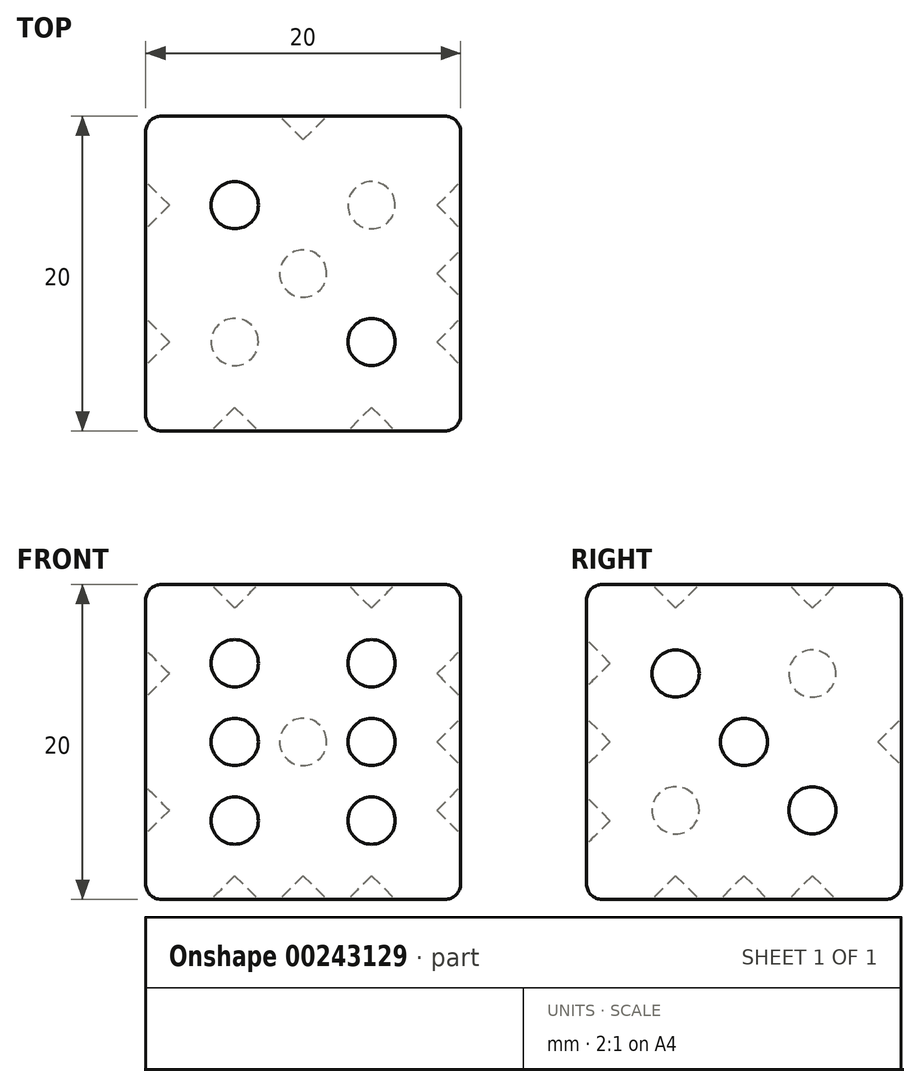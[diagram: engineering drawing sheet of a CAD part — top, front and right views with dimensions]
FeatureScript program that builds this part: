
annotation { "Feature Type Name" : "Feature", "Feature Type Description" : "" }
export const myFeature = defineFeature(function(context is Context, id is Id, definition is map)
    precondition{}
    {
        {
            var Q0;
            Q0=qCreatedBy(makeId("Top.planeOp"),FACE);
            var sketch = newSketch(context, id + "F0", { "sketchPlane" : qUnion([Q0])});
            skLineSegment(sketch, "E0.bottom", {"start": v(0, 0) * mm, "end": v(20, 0) * mm});
            skLineSegment(sketch, "E0.top", {"start": v(0, 20) * mm, "end": v(20, 20) * mm});
            skLineSegment(sketch, "E0.left", {"start": v(0, 0) * mm, "end": v(0, 20) * mm});
            skLineSegment(sketch, "E0.right", {"start": v(20, 0) * mm, "end": v(20, 20) * mm});
            skSolve(sketch);
        }
        {
            var Q0;
            Q0 = qSketchRegion(id + "F0", true);
            extrude(context, id + "F1", {"entities" : qUnion([Q0]), "depth" : 20 * mm});
        }
        {
            var Q0;
            Q0=makeQuery(id+"F1.opExtrude","CAP_FACE",FACE,{"disambiguationData":[OSD([sQuery(id+"F0.wireOp",EDGE,"E0.bottom"),sQuery(id+"F0.wireOp",EDGE,"E0.top"),sQuery(id+"F0.wireOp",EDGE,"E0.left"),sQuery(id+"F0.wireOp",EDGE,"E0.right")])],"isStart":false});
            var sketch = newSketch(context, id + "F2", { "sketchPlane" : qUnion([Q0])});
            skLineSegment(sketch, "E1", {"start": v(0, 20) * mm, "end": v(5.66, 14.34) * mm, "construction": true});
            skLineSegment(sketch, "E2", {"start": v(20, 0) * mm, "end": v(14.34, 5.66) * mm, "construction": true});
            skCircle(sketch, "E3", {"center": v(5.66, 14.34) * mm, "radius": 1.5 * mm});
            skCircle(sketch, "E4", {"center": v(14.34, 5.66) * mm, "radius": 1.5 * mm});
            skSolve(sketch);
        }
        {
            var Q0;
            Q0 = qSketchRegion(id + "F2", true);
            extrude(context, id + "F3", {"entities" : qUnion([Q0]), "operationType" : NewBodyOperationType.REMOVE, "oppositeDirection" : true, "depth" : 1.5 * mm});
        }
        {
            var Q0;
            Q0=makeQuery(id+"F1.opExtrude","CAP_EDGE",EDGE,{"disambiguationData":[OSD([sQuery(id+"F0.wireOp",EDGE,"E0.bottom")])],"isStart":false});
            var Q1;
            Q1=makeQuery(id+"F1.opExtrude","SWEPT_EDGE",EDGE,{"disambiguationData":[OSD([sQuery(id+"F0.wireOp",EDGE,"E0.bottom"),sQuery(id+"F0.wireOp",EDGE,"E0.right")])]});
            var Q2;
            Q2=makeQuery(id+"F1.opExtrude","SWEPT_EDGE",EDGE,{"disambiguationData":[OSD([sQuery(id+"F0.wireOp",EDGE,"E0.bottom"),sQuery(id+"F0.wireOp",EDGE,"E0.left")])]});
            var Q3;
            Q3=makeQuery(id+"F1.opExtrude","CAP_EDGE",EDGE,{"disambiguationData":[OSD([sQuery(id+"F0.wireOp",EDGE,"E0.left")])],"isStart":true});
            var Q4;
            Q4=makeQuery(id+"F1.opExtrude","CAP_EDGE",EDGE,{"disambiguationData":[OSD([sQuery(id+"F0.wireOp",EDGE,"E0.left")])],"isStart":false});
            var Q5;
            Q5=makeQuery(id+"F1.opExtrude","CAP_EDGE",EDGE,{"disambiguationData":[OSD([sQuery(id+"F0.wireOp",EDGE,"E0.top")])],"isStart":false});
            var Q6;
            Q6=makeQuery(id+"F1.opExtrude","SWEPT_EDGE",EDGE,{"disambiguationData":[OSD([sQuery(id+"F0.wireOp",EDGE,"E0.top"),sQuery(id+"F0.wireOp",EDGE,"E0.right")])]});
            var Q7;
            Q7=makeQuery(id+"F1.opExtrude","CAP_EDGE",EDGE,{"disambiguationData":[OSD([sQuery(id+"F0.wireOp",EDGE,"E0.right")])],"isStart":false});
            var Q8;
            Q8=makeQuery(id+"F1.opExtrude","CAP_EDGE",EDGE,{"disambiguationData":[OSD([sQuery(id+"F0.wireOp",EDGE,"E0.top")])],"isStart":true});
            var Q9;
            Q9=makeQuery(id+"F1.opExtrude","CAP_EDGE",EDGE,{"disambiguationData":[OSD([sQuery(id+"F0.wireOp",EDGE,"E0.right")])],"isStart":true});
            var Q10;
            Q10=makeQuery(id+"F1.opExtrude","SWEPT_EDGE",EDGE,{"disambiguationData":[OSD([sQuery(id+"F0.wireOp",EDGE,"E0.top"),sQuery(id+"F0.wireOp",EDGE,"E0.left")])]});
            var Q11;
            Q11=makeQuery(id+"F1.opExtrude","CAP_EDGE",EDGE,{"disambiguationData":[OSD([sQuery(id+"F0.wireOp",EDGE,"E0.bottom")])],"isStart":true});
            fillet(context, id + "F4", {"entities" : qUnion([Q0, Q1, Q2, Q3, Q4, Q5, Q6, Q7, Q8, Q9, Q10, Q11]), "radius" : 1 * mm, "tangentPropagation" : true, "allowEdgeOverflow" : false});
        }
        {
            var Q0;
            Q0=makeQuery(id+"Fp3urKfKEuPVBoE_1.boolean.opBoolean","COPY",FACE,{"derivedFrom":makeQuery(id+"Fp3urKfKEuPVBoE_1.opExtrude","CAP_FACE",FACE,{"disambiguationData":[OSD([sQuery(id+"FZp8JHhIHyCAixJ_1.wireOp",EDGE,"yZyBnYss-4Vlz-teav-fmUy-BsDWVrtYF5FO")])],"isStart":false})});
            var Q1;
            Q1=makeQuery(id+"F3.boolean.opBoolean","COPY",FACE,{"derivedFrom":makeQuery(id+"F3.opExtrude","CAP_FACE",FACE,{"disambiguationData":[OSD([sQuery(id+"F2.wireOp",EDGE,"E4")])],"isStart":false})});
            var Q2;
            Q2=makeQuery(id+"F3.boolean.opBoolean","COPY",EDGE,{"derivedFrom":makeQuery(id+"F3.opExtrude","CAP_EDGE",EDGE,{"disambiguationData":[OSD([sQuery(id+"F2.wireOp",EDGE,"E3")])],"isStart":false})});
            chamfer(context, id + "F5", {"entities" : qUnion([Q0, Q1, Q2]), "width" : 1.5 * mm, "tangentPropagation" : true});
        }
        {
            var Q0;
            Q0=makeQuery(id+"F1.opExtrude","CAP_FACE",FACE,{"disambiguationData":[OSD([sQuery(id+"F0.wireOp",EDGE,"E0.bottom"),sQuery(id+"F0.wireOp",EDGE,"E0.top"),sQuery(id+"F0.wireOp",EDGE,"E0.left"),sQuery(id+"F0.wireOp",EDGE,"E0.right")])],"isStart":true});
            var sketch = newSketch(context, id + "F6", { "sketchPlane" : qUnion([Q0])});
            skLineSegment(sketch, "E5", {"start": v(0, 0) * mm, "end": v(5.66, -5.66) * mm, "construction": true});
            skLineSegment(sketch, "E6", {"start": v(20, 0) * mm, "end": v(14.34, -5.66) * mm, "construction": true});
            skPoint(sketch, "E7", {"position": v(5.66, -5.66) * mm});
            skPoint(sketch, "E8", {"position": v(14.34, -14.34) * mm});
            skPoint(sketch, "E9", {"position": v(14.34, -5.66) * mm});
            skPoint(sketch, "E10", {"position": v(5.66, -14.34) * mm});
            skLineSegment(sketch, "E11.trimOffspring", {"start": v(14.34, -14.34) * mm, "end": v(20, -20) * mm, "construction": true});
            skLineSegment(sketch, "E12.trimOffspring", {"start": v(5.66, -14.34) * mm, "end": v(0, -20) * mm, "construction": true});
            skCircle(sketch, "E13", {"center": v(5.66, -5.66) * mm, "radius": 1.5 * mm});
            skCircle(sketch, "E14", {"center": v(14.34, -5.66) * mm, "radius": 1.5 * mm});
            skCircle(sketch, "E15", {"center": v(14.34, -14.34) * mm, "radius": 1.5 * mm});
            skCircle(sketch, "E16", {"center": v(5.66, -14.34) * mm, "radius": 1.5 * mm});
            skLineSegment(sketch, "E17", {"start": v(5.66, -5.66) * mm, "end": v(14.34, -14.34) * mm, "construction": true});
            skCircle(sketch, "E18", {"center": v(10, -10) * mm, "radius": 1.5 * mm});
            skSolve(sketch);
        }
        {
            var Q0;
            Q0 = qSketchRegion(id + "F6", true);
            extrude(context, id + "F7", {"entities" : qUnion([Q0]), "operationType" : NewBodyOperationType.REMOVE, "oppositeDirection" : true, "depth" : 1.5 * mm});
        }
        {
            var Q0;
            Q0=makeQuery(id+"F7.boolean.opBoolean","COPY",FACE,{"derivedFrom":makeQuery(id+"F7.opExtrude","CAP_FACE",FACE,{"disambiguationData":[OSD([sQuery(id+"F6.wireOp",EDGE,"E13")])],"isStart":false})});
            var Q1;
            Q1=makeQuery(id+"F7.boolean.opBoolean","COPY",FACE,{"derivedFrom":makeQuery(id+"F7.opExtrude","CAP_FACE",FACE,{"disambiguationData":[OSD([sQuery(id+"F6.wireOp",EDGE,"E14")])],"isStart":false})});
            var Q2;
            Q2=makeQuery(id+"F7.boolean.opBoolean","COPY",FACE,{"derivedFrom":makeQuery(id+"F7.opExtrude","CAP_FACE",FACE,{"disambiguationData":[OSD([sQuery(id+"F6.wireOp",EDGE,"E18")])],"isStart":false})});
            var Q3;
            Q3=makeQuery(id+"F7.boolean.opBoolean","COPY",FACE,{"derivedFrom":makeQuery(id+"F7.opExtrude","CAP_FACE",FACE,{"disambiguationData":[OSD([sQuery(id+"F6.wireOp",EDGE,"E15")])],"isStart":false})});
            var Q4;
            Q4=makeQuery(id+"F7.boolean.opBoolean","COPY",FACE,{"derivedFrom":makeQuery(id+"F7.opExtrude","CAP_FACE",FACE,{"disambiguationData":[OSD([sQuery(id+"F6.wireOp",EDGE,"E16")])],"isStart":false})});
            chamfer(context, id + "F8", {"entities" : qUnion([Q0, Q1, Q2, Q3, Q4]), "width" : 1.5 * mm, "tangentPropagation" : true});
        }
        {
            var Q0;
            Q0=makeQuery(id+"F1.opExtrude","SWEPT_FACE",FACE,{"disambiguationData":[OSD([sQuery(id+"F0.wireOp",EDGE,"E0.right")])]});
            var sketch = newSketch(context, id + "F9", { "sketchPlane" : qUnion([Q0])});
            skLineSegment(sketch, "E19", {"start": v(0, 20) * mm, "end": v(20, 0) * mm, "construction": true});
            skPoint(sketch, "E20", {"position": v(5.66, 14.34) * mm});
            skPoint(sketch, "E21", {"position": v(14.34, 5.66) * mm});
            skCircle(sketch, "E22", {"center": v(5.66, 14.34) * mm, "radius": 1.5 * mm});
            skCircle(sketch, "E23", {"center": v(14.34, 5.66) * mm, "radius": 1.5 * mm});
            skCircle(sketch, "E24", {"center": v(10, 10) * mm, "radius": 1.5 * mm});
            skSolve(sketch);
        }
        {
            var Q0;
            Q0 = qSketchRegion(id + "F9", true);
            extrude(context, id + "F10", {"entities" : qUnion([Q0]), "operationType" : NewBodyOperationType.REMOVE, "oppositeDirection" : true, "depth" : 1.5 * mm});
        }
        {
            var Q0;
            Q0=makeQuery(id+"F10.boolean.opBoolean","COPY",FACE,{"derivedFrom":makeQuery(id+"F10.opExtrude","CAP_FACE",FACE,{"disambiguationData":[OSD([sQuery(id+"F9.wireOp",EDGE,"E22")])],"isStart":false})});
            var Q1;
            Q1=makeQuery(id+"F10.boolean.opBoolean","COPY",FACE,{"derivedFrom":makeQuery(id+"F10.opExtrude","CAP_FACE",FACE,{"disambiguationData":[OSD([sQuery(id+"F9.wireOp",EDGE,"E24")])],"isStart":false})});
            var Q2;
            Q2=makeQuery(id+"F10.boolean.opBoolean","COPY",FACE,{"derivedFrom":makeQuery(id+"F10.opExtrude","CAP_FACE",FACE,{"disambiguationData":[OSD([sQuery(id+"F9.wireOp",EDGE,"E23")])],"isStart":false})});
            chamfer(context, id + "F11", {"entities" : qUnion([Q0, Q1, Q2]), "width" : 1.5 * mm, "tangentPropagation" : true});
        }
        {
            var Q0;
            Q0=makeQuery(id+"F1.opExtrude","SWEPT_FACE",FACE,{"disambiguationData":[OSD([sQuery(id+"F0.wireOp",EDGE,"E0.top")])]});
            var sketch = newSketch(context, id + "F12", { "sketchPlane" : qUnion([Q0])});
            skLineSegment(sketch, "E25", {"start": v(-20, 20) * mm, "end": v(0, 0) * mm, "construction": true});
            skCircle(sketch, "E26", {"center": v(-10, 10) * mm, "radius": 1.5 * mm});
            skSolve(sketch);
        }
        {
            var Q0;
            Q0 = qSketchRegion(id + "F12", true);
            extrude(context, id + "F13", {"entities" : qUnion([Q0]), "operationType" : NewBodyOperationType.REMOVE, "oppositeDirection" : true, "depth" : 1.5 * mm});
        }
        {
            var Q0;
            Q0=makeQuery(id+"F13.boolean.opBoolean","COPY",FACE,{"derivedFrom":makeQuery(id+"F13.opExtrude","CAP_FACE",FACE,{"disambiguationData":[OSD([sQuery(id+"F12.wireOp",EDGE,"E26")])],"isStart":false})});
            chamfer(context, id + "F14", {"entities" : qUnion([Q0]), "width" : 1.5 * mm, "tangentPropagation" : true});
        }
        {
            var Q0;
            Q0=makeQuery(id+"F1.opExtrude","SWEPT_FACE",FACE,{"disambiguationData":[OSD([sQuery(id+"F0.wireOp",EDGE,"E0.left")])]});
            var sketch = newSketch(context, id + "F15", { "sketchPlane" : qUnion([Q0])});
            skLineSegment(sketch, "E27", {"start": v(-20, 20) * mm, "end": v(-14.34, 14.34) * mm, "construction": true});
            skLineSegment(sketch, "E28", {"start": v(0, 20) * mm, "end": v(-5.66, 14.34) * mm, "construction": true});
            skPoint(sketch, "E29", {"position": v(-14.34, 14.34) * mm});
            skPoint(sketch, "E30", {"position": v(-5.66, 5.66) * mm});
            skPoint(sketch, "E31", {"position": v(-5.66, 14.34) * mm});
            skPoint(sketch, "E32", {"position": v(-14.34, 5.66) * mm});
            skLineSegment(sketch, "E33.trimOffspring", {"start": v(-5.66, 5.66) * mm, "end": v(0, 0) * mm, "construction": true});
            skLineSegment(sketch, "E34.trimOffspring", {"start": v(-14.34, 5.66) * mm, "end": v(-20, 0) * mm, "construction": true});
            skCircle(sketch, "E35", {"center": v(-14.34, 14.34) * mm, "radius": 1.5 * mm});
            skCircle(sketch, "E36", {"center": v(-5.66, 14.34) * mm, "radius": 1.5 * mm});
            skCircle(sketch, "E37", {"center": v(-5.66, 5.66) * mm, "radius": 1.5 * mm});
            skCircle(sketch, "E38", {"center": v(-14.34, 5.66) * mm, "radius": 1.5 * mm});
            skSolve(sketch);
        }
        {
            var Q0;
            Q0 = qSketchRegion(id + "F15", true);
            extrude(context, id + "F16", {"entities" : qUnion([Q0]), "operationType" : NewBodyOperationType.REMOVE, "oppositeDirection" : true, "depth" : 1.5 * mm});
        }
        {
            var Q0;
            Q0=makeQuery(id+"F16.boolean.opBoolean","COPY",FACE,{"derivedFrom":makeQuery(id+"F16.opExtrude","CAP_FACE",FACE,{"disambiguationData":[OSD([sQuery(id+"F15.wireOp",EDGE,"E35")])],"isStart":false})});
            var Q1;
            Q1=makeQuery(id+"F16.boolean.opBoolean","COPY",FACE,{"derivedFrom":makeQuery(id+"F16.opExtrude","CAP_FACE",FACE,{"disambiguationData":[OSD([sQuery(id+"F15.wireOp",EDGE,"E36")])],"isStart":false})});
            var Q2;
            Q2=makeQuery(id+"F16.boolean.opBoolean","COPY",FACE,{"derivedFrom":makeQuery(id+"F16.opExtrude","CAP_FACE",FACE,{"disambiguationData":[OSD([sQuery(id+"F15.wireOp",EDGE,"E37")])],"isStart":false})});
            var Q3;
            Q3=makeQuery(id+"F16.boolean.opBoolean","COPY",EDGE,{"derivedFrom":makeQuery(id+"F16.opExtrude","CAP_EDGE",EDGE,{"disambiguationData":[OSD([sQuery(id+"F15.wireOp",EDGE,"E38")])],"isStart":false})});
            chamfer(context, id + "F17", {"entities" : qUnion([Q0, Q1, Q2, Q3]), "width" : 1.5 * mm, "tangentPropagation" : true});
        }
        {
            var Q0;
            Q0=makeQuery(id+"F1.opExtrude","SWEPT_FACE",FACE,{"disambiguationData":[OSD([sQuery(id+"F0.wireOp",EDGE,"E0.bottom")])]});
            var sketch = newSketch(context, id + "F18", { "sketchPlane" : qUnion([Q0])});
            skLineSegment(sketch, "E39", {"start": v(5.66, 10) * mm, "end": v(5.66, 5) * mm, "construction": true});
            skLineSegment(sketch, "E40", {"start": v(5.66, 5) * mm, "end": v(5.66, 0) * mm, "construction": true});
            skLineSegment(sketch, "E41", {"start": v(14.34, 0) * mm, "end": v(14.34, 5) * mm, "construction": true});
            skLineSegment(sketch, "E42", {"start": v(14.34, 5) * mm, "end": v(14.34, 10) * mm, "construction": true});
            skCircle(sketch, "E43", {"center": v(5.66, 10) * mm, "radius": 1.5 * mm});
            skCircle(sketch, "E44", {"center": v(5.66, 5) * mm, "radius": 1.5 * mm});
            skCircle(sketch, "E45", {"center": v(14.34, 10) * mm, "radius": 1.5 * mm});
            skCircle(sketch, "E46", {"center": v(14.34, 5) * mm, "radius": 1.5 * mm});
            skLineSegment(sketch, "E47", {"start": v(5.66, 10) * mm, "end": v(5.66, 15) * mm, "construction": true});
            skLineSegment(sketch, "E48", {"start": v(14.34, 10) * mm, "end": v(14.34, 15) * mm, "construction": true});
            skCircle(sketch, "E49", {"center": v(5.66, 15) * mm, "radius": 1.5 * mm});
            skCircle(sketch, "E50", {"center": v(14.34, 15) * mm, "radius": 1.5 * mm});
            skSolve(sketch);
        }
        {
            var Q0;
            Q0 = qSketchRegion(id + "F18", true);
            extrude(context, id + "F19", {"entities" : qUnion([Q0]), "operationType" : NewBodyOperationType.REMOVE, "oppositeDirection" : true, "depth" : 1.5 * mm});
        }
        {
            var Q0;
            Q0=makeQuery(id+"F19.boolean.opBoolean","COPY",FACE,{"derivedFrom":makeQuery(id+"F19.opExtrude","CAP_FACE",FACE,{"disambiguationData":[OSD([sQuery(id+"F18.wireOp",EDGE,"E49")])],"isStart":false})});
            var Q1;
            Q1=makeQuery(id+"F19.boolean.opBoolean","COPY",FACE,{"derivedFrom":makeQuery(id+"F19.opExtrude","CAP_FACE",FACE,{"disambiguationData":[OSD([sQuery(id+"F18.wireOp",EDGE,"E50")])],"isStart":false})});
            var Q2;
            Q2=makeQuery(id+"F19.boolean.opBoolean","COPY",EDGE,{"derivedFrom":makeQuery(id+"F19.opExtrude","CAP_EDGE",EDGE,{"disambiguationData":[OSD([sQuery(id+"F18.wireOp",EDGE,"E45")])],"isStart":false})});
            var Q3;
            Q3=makeQuery(id+"F19.boolean.opBoolean","COPY",FACE,{"derivedFrom":makeQuery(id+"F19.opExtrude","CAP_FACE",FACE,{"disambiguationData":[OSD([sQuery(id+"F18.wireOp",EDGE,"E43")])],"isStart":false})});
            var Q4;
            Q4=makeQuery(id+"F19.boolean.opBoolean","COPY",EDGE,{"derivedFrom":makeQuery(id+"F19.opExtrude","CAP_EDGE",EDGE,{"disambiguationData":[OSD([sQuery(id+"F18.wireOp",EDGE,"E46")])],"isStart":false})});
            var Q5;
            Q5=makeQuery(id+"F19.boolean.opBoolean","COPY",EDGE,{"derivedFrom":makeQuery(id+"F19.opExtrude","CAP_EDGE",EDGE,{"disambiguationData":[OSD([sQuery(id+"F18.wireOp",EDGE,"E44")])],"isStart":false})});
            chamfer(context, id + "F20", {"entities" : qUnion([Q0, Q1, Q2, Q3, Q4, Q5]), "width" : 1.5 * mm, "tangentPropagation" : true});
        }
    });
